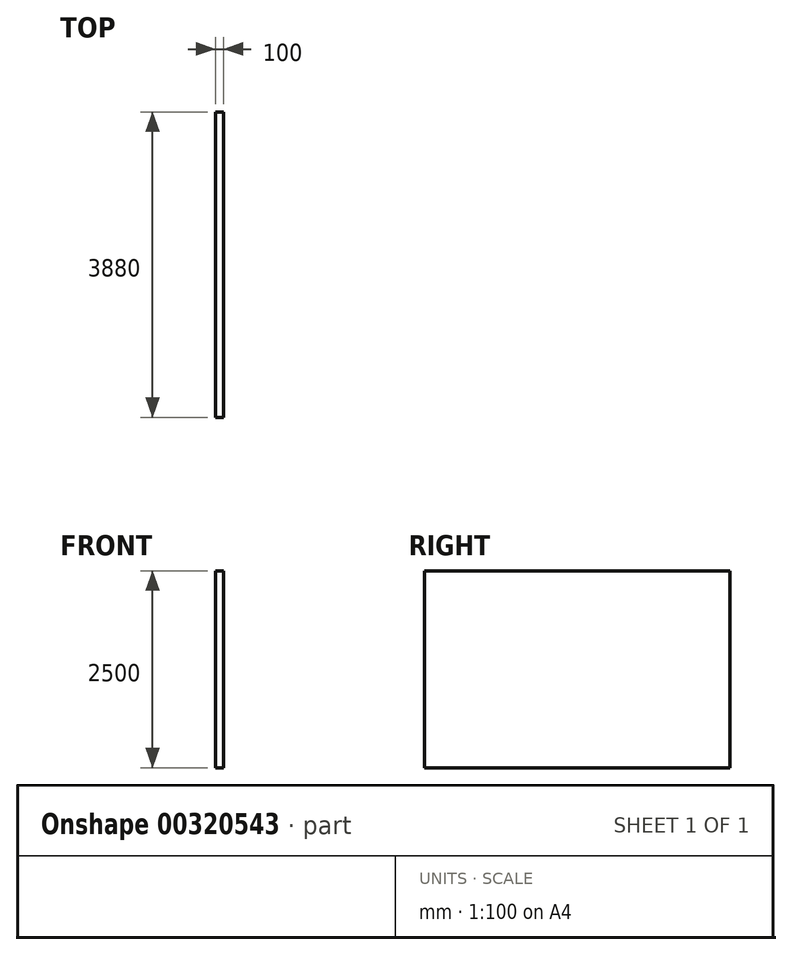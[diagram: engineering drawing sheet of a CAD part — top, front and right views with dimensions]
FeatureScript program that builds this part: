
annotation { "Feature Type Name" : "Feature", "Feature Type Description" : "" }
export const myFeature = defineFeature(function(context is Context, id is Id, definition is map)
    precondition{}
    {
        {
            var Q0;
            Q0=qCreatedBy(makeId("Right.planeOp"),FACE);
            var sketch = newSketch(context, id + "F0", { "sketchPlane" : qUnion([Q0])});
            skLineSegment(sketch, "E0.bottom", {"start": v(1940, 1250) * mm, "end": v(-1940, 1250) * mm});
            skLineSegment(sketch, "E0.top", {"start": v(1940, -1250) * mm, "end": v(-1940, -1250) * mm});
            skLineSegment(sketch, "E0.left", {"start": v(1940, 1250) * mm, "end": v(1940, -1250) * mm});
            skLineSegment(sketch, "E0.right", {"start": v(-1940, 1250) * mm, "end": v(-1940, -1250) * mm});
            skPoint(sketch, "E0.middle", {"position": v(0, 0) * mm});
            skSolve(sketch);
        }
        {
            var Q0;
            Q0=makeQuery(id+"F0.imprint","IMPRINT",FACE,{"disambiguationData":[TD([[makeQuery(id+"F0.imprint","IMPRINT",EDGE,{"derivedFrom":sQuery(id+"F0.wireOp",EDGE,"E0.bottom")}),1.0]])]});
            extrude(context, id + "F1", {"entities" : qUnion([Q0]), "oppositeDirection" : true, "depth" : 100 * mm});
        }
    });
